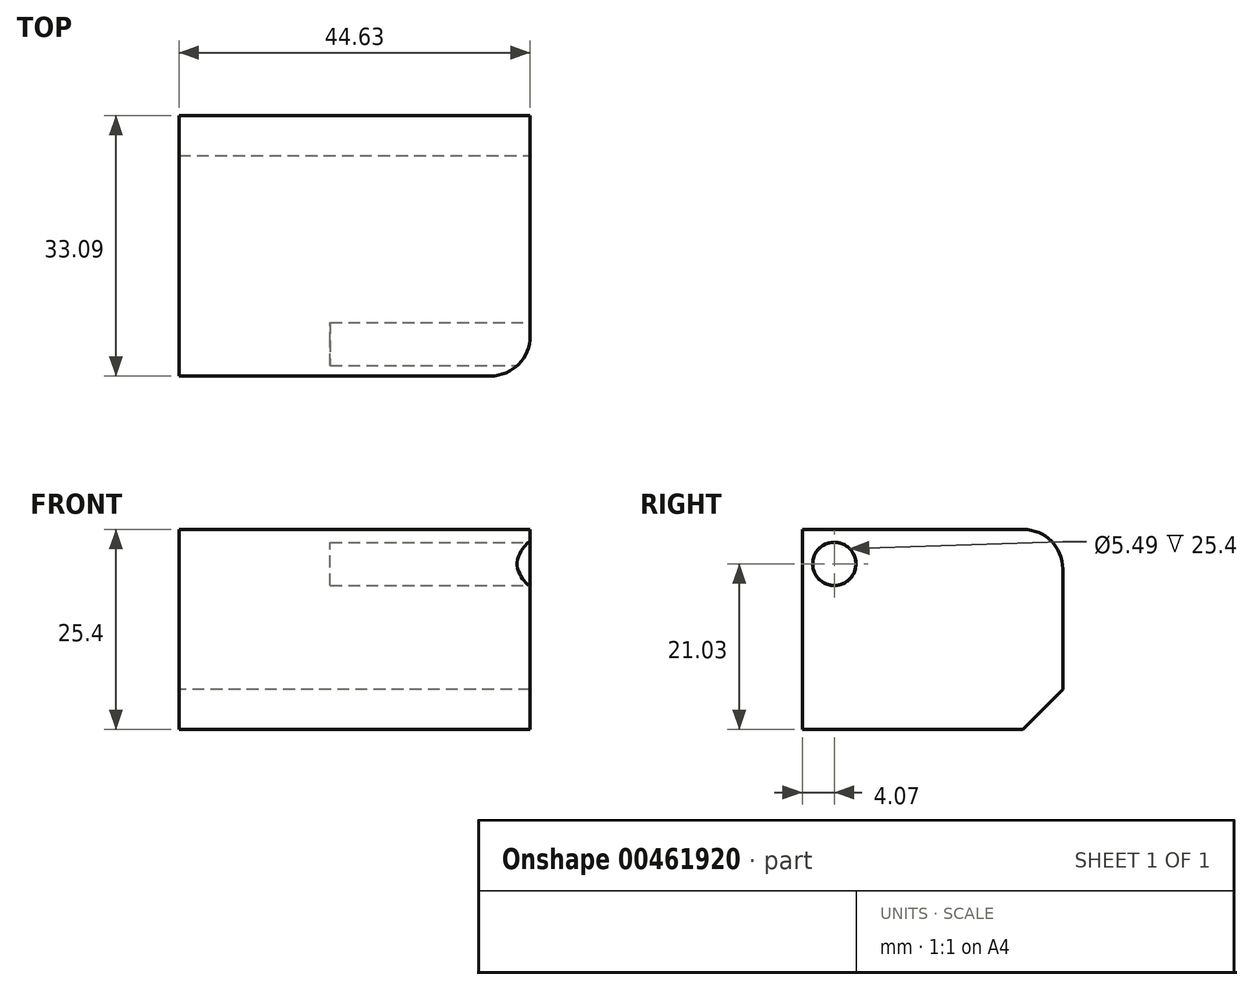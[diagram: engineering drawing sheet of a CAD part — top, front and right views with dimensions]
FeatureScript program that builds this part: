
annotation { "Feature Type Name" : "Feature", "Feature Type Description" : "" }
export const myFeature = defineFeature(function(context is Context, id is Id, definition is map)
    precondition{}
    {
        {
            var Q0;
            Q0=qCreatedBy(makeId("Top.planeOp"),FACE);
            var sketch = newSketch(context, id + "F0", { "sketchPlane" : qUnion([Q0])});
            skLineSegment(sketch, "E0.bottom", {"start": v(0, 0) * mm, "end": v(44.63, 0) * mm});
            skLineSegment(sketch, "E0.top", {"start": v(0, -33.1) * mm, "end": v(44.63, -33.1) * mm});
            skLineSegment(sketch, "E0.left", {"start": v(0, 0) * mm, "end": v(0, -33.1) * mm});
            skLineSegment(sketch, "E0.right", {"start": v(44.63, 0) * mm, "end": v(44.63, -33.1) * mm});
            skSolve(sketch);
        }
        {
            var Q0;
            Q0 = qSketchRegion(id + "F0", true);
            extrude(context, id + "F1", {"entities" : qUnion([Q0]), "depth" : 25.4 * mm});
        }
        {
            var Q0;
            Q0=makeQuery(id+"F1.opExtrude","CAP_EDGE",EDGE,{"disambiguationData":[OSD([sQuery(id+"F0.wireOp",EDGE,"E0.bottom")])],"isStart":false});
            fillet(context, id + "F2", {"entities" : qUnion([Q0]), "radius" : 5 * mm, "tangentPropagation" : true, "allowEdgeOverflow" : false});
        }
        {
            var Q0;
            Q0=makeQuery(id+"F1.opExtrude","CAP_EDGE",EDGE,{"disambiguationData":[OSD([sQuery(id+"F0.wireOp",EDGE,"E0.bottom")])],"isStart":true});
            chamfer(context, id + "F3", {"entities" : qUnion([Q0]), "width" : 5.08 * mm, "tangentPropagation" : true});
        }
        {
            var Q0;
            Q0=makeQuery(id+"F1.opExtrude","SWEPT_FACE",FACE,{"disambiguationData":[OSD([sQuery(id+"F0.wireOp",EDGE,"E0.right")])]});
            var sketch = newSketch(context, id + "F4", { "sketchPlane" : qUnion([Q0])});
            skCircle(sketch, "E1", {"center": v(-29.02, 21.03) * mm, "radius": 2.75 * mm});
            skSolve(sketch);
        }
        {
            var Q0;
            Q0 = qSketchRegion(id + "F4", true);
            extrude(context, id + "F5", {"entities" : qUnion([Q0]), "operationType" : NewBodyOperationType.REMOVE, "oppositeDirection" : true, "depth" : 25.4 * mm});
        }
        {
            var Q0;
            Q0=makeQuery(id+"F1.opExtrude","SWEPT_EDGE",EDGE,{"disambiguationData":[OSD([sQuery(id+"F0.wireOp",EDGE,"E0.top"),sQuery(id+"F0.wireOp",EDGE,"E0.right")])]});
            fillet(context, id + "F6", {"entities" : qUnion([Q0]), "radius" : 5.08 * mm, "tangentPropagation" : true, "allowEdgeOverflow" : false});
        }
    });
